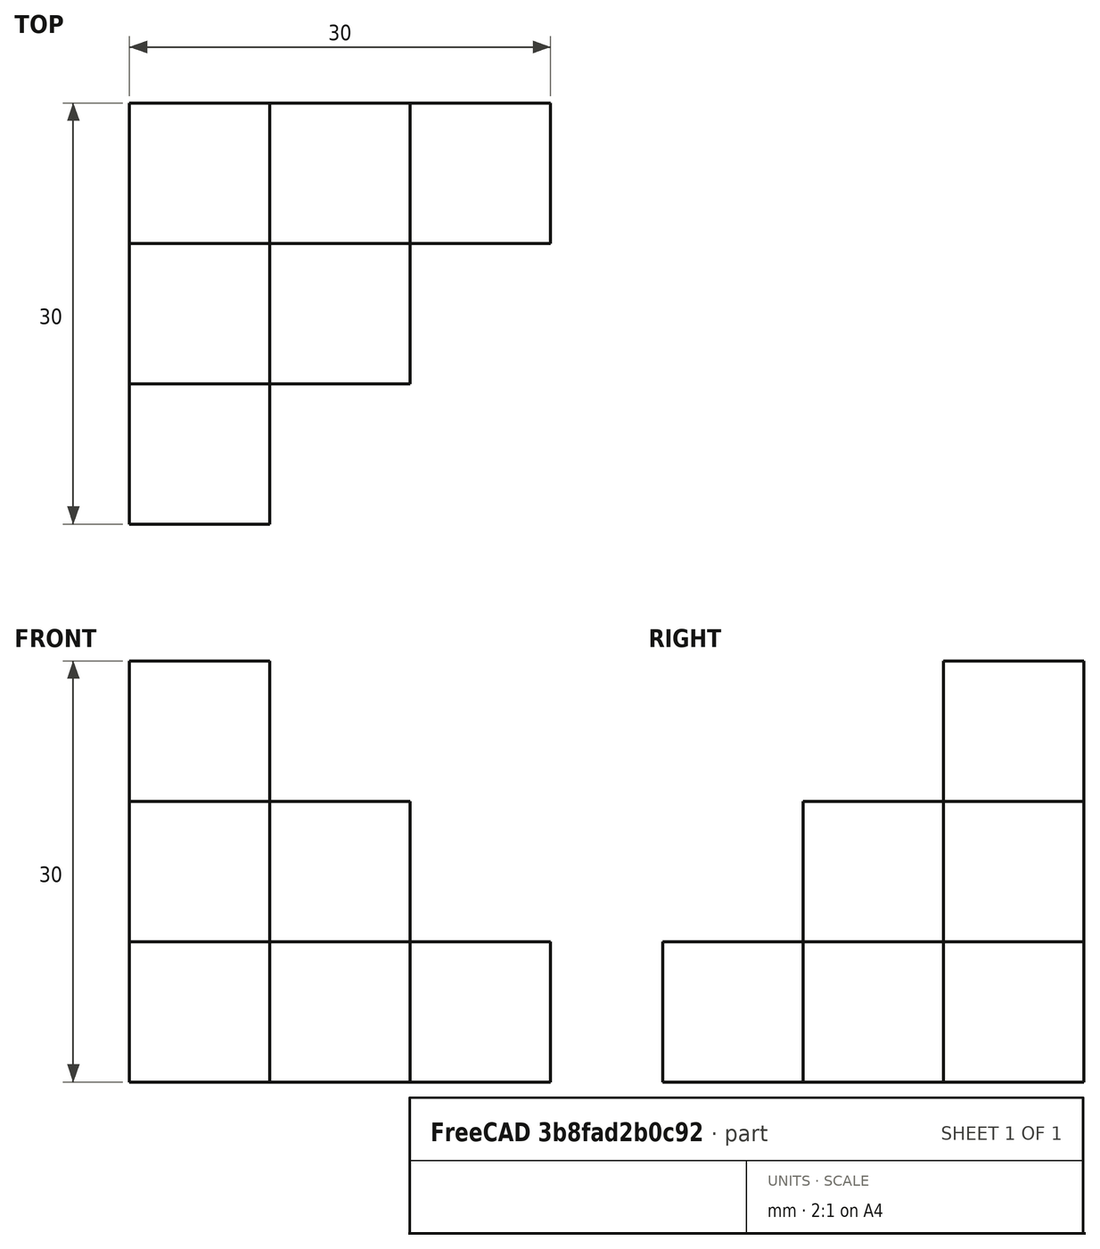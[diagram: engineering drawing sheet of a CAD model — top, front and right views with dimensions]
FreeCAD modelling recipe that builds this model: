
FCSTD DOCUMENT  (FreeCAD 0.20R29177 (Git))
Label: EjercicioVideo3
License: All rights reserved
LicenseURL: http://en.wikipedia.org/wiki/All_rights_reserved
objects: Part::Box×6
note: 6 computed .brp shape members not serialized (recipe doc carries the construction recipe); baked Part::Feature solids carry a one-line shape summary decoded from their .brp

FEATURE [Part::Box] Box  label="Nivel1-Cubo1"
  AttacherType = Attacher::AttachEngine3D
  Height = 10
  Length = 10
  Width = 10
FEATURE [Part::Box] Box001  label="Nivel2-Cubo1"
  AttacherType = Attacher::AttachEngine3D
  Height = 10
  Length = 10
  Placement = pos=(10,0,-10) rot=(0,0,1;0rad)
  Width = 10
FEATURE [Part::Box] Box002  label="Nivel2-Cubo2"
  AttacherType = Attacher::AttachEngine3D
  Height = 10
  Length = 10
  Placement = pos=(0,-10,-10) rot=(0,0,1;0rad)
  Width = 10
FEATURE [Part::Box] Box003  label="Nivel3-Cubo1"
  AttacherType = Attacher::AttachEngine3D
  Height = 10
  Length = 10
  Placement = pos=(0,-20,-20) rot=(0,0,1;0rad)
  Width = 10
FEATURE [Part::Box] Box004  label="Nivel3-Cubo2"
  AttacherType = Attacher::AttachEngine3D
  Height = 10
  Length = 10
  Placement = pos=(10,-10,-20) rot=(0,0,1;0rad)
  Width = 10
FEATURE [Part::Box] Box005  label="Nivel3-Cubo3"
  AttacherType = Attacher::AttachEngine3D
  Height = 10
  Length = 10
  Placement = pos=(20,0,-20) rot=(0,0,1;0rad)
  Width = 10
